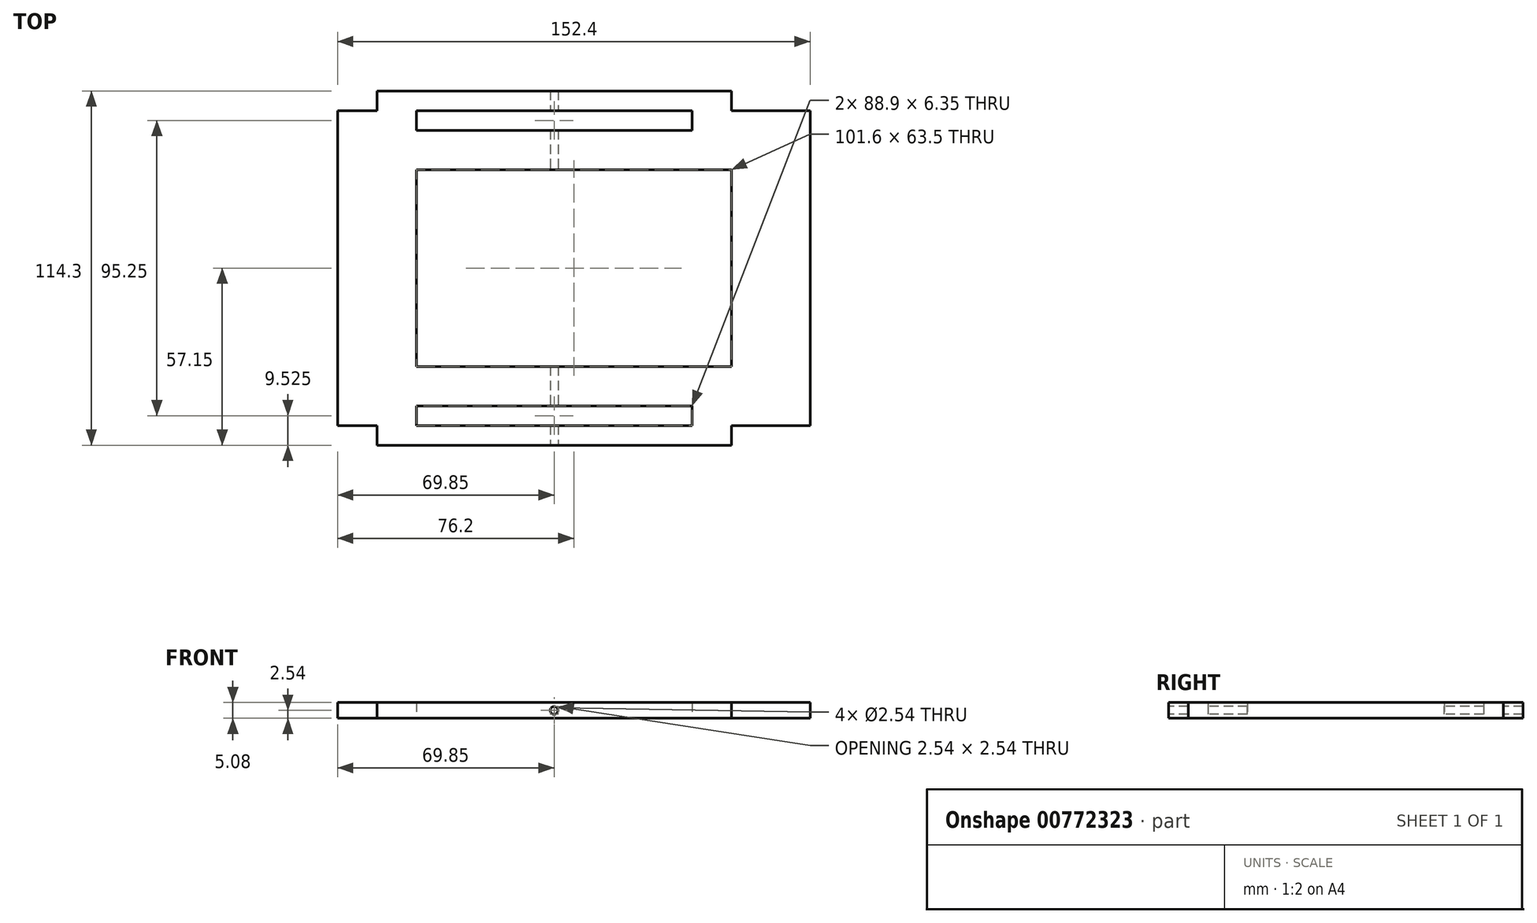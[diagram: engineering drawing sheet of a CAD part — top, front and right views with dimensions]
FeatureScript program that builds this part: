
annotation { "Feature Type Name" : "Feature", "Feature Type Description" : "" }
export const myFeature = defineFeature(function(context is Context, id is Id, definition is map)
    precondition{}
    {
        {
            var Q0;
            Q0=qCreatedBy(makeId("Top.planeOp"),FACE);
            var sketch = newSketch(context, id + "F0", { "sketchPlane" : qUnion([Q0])});
            skLineSegment(sketch, "E0", {"start": v(-76.2, 0) * mm, "end": v(-76.2, 50.8) * mm});
            skLineSegment(sketch, "E1", {"start": v(76.2, 0) * mm, "end": v(76.2, 50.8) * mm});
            skLineSegment(sketch, "E2", {"start": v(-76.2, 0) * mm, "end": v(-76.2, -50.8) * mm});
            skLineSegment(sketch, "E3", {"start": v(76.2, 0) * mm, "end": v(76.2, -50.8) * mm});
            skLineSegment(sketch, "E4", {"start": v(-76.2, -50.8) * mm, "end": v(76.2, -50.8) * mm});
            skLineSegment(sketch, "E5", {"start": v(-76.2, 50.8) * mm, "end": v(76.2, 50.8) * mm});
            skPoint(sketch, "E6", {"position": v(-50.8, -50.8) * mm});
            skPoint(sketch, "E7", {"position": v(38.1, -50.8) * mm});
            skLineSegment(sketch, "E8", {"start": v(-50.8, -50.8) * mm, "end": v(-50.8, -44.45) * mm});
            skLineSegment(sketch, "E9", {"start": v(-50.8, -44.45) * mm, "end": v(38.1, -44.45) * mm});
            skLineSegment(sketch, "E10", {"start": v(38.1, -44.45) * mm, "end": v(38.1, -50.8) * mm});
            skPoint(sketch, "E11", {"position": v(-50.8, 50.8) * mm});
            skPoint(sketch, "E12", {"position": v(38.1, 50.8) * mm});
            skLineSegment(sketch, "E13", {"start": v(-50.8, 50.8) * mm, "end": v(-50.8, 44.45) * mm});
            skLineSegment(sketch, "E14", {"start": v(-50.8, 44.45) * mm, "end": v(38.1, 44.45) * mm});
            skLineSegment(sketch, "E15", {"start": v(38.1, 50.8) * mm, "end": v(38.1, 44.45) * mm});
            skPoint(sketch, "E16", {"position": v(-63.5, -50.8) * mm});
            skPoint(sketch, "E17", {"position": v(50.8, -50.8) * mm});
            skPoint(sketch, "E18", {"position": v(-63.5, 50.8) * mm});
            skPoint(sketch, "E19", {"position": v(50.8, 50.8) * mm});
            skLineSegment(sketch, "E20", {"start": v(-63.5, -50.8) * mm, "end": v(-63.5, -57.15) * mm});
            skLineSegment(sketch, "E21", {"start": v(-63.5, 50.8) * mm, "end": v(-63.5, 57.15) * mm});
            skLineSegment(sketch, "E22", {"start": v(50.8, 50.8) * mm, "end": v(50.8, 57.15) * mm});
            skLineSegment(sketch, "E23", {"start": v(50.8, -50.8) * mm, "end": v(50.8, -57.15) * mm});
            skLineSegment(sketch, "E24", {"start": v(-63.5, 57.15) * mm, "end": v(50.8, 57.15) * mm});
            skLineSegment(sketch, "E25", {"start": v(-63.5, -57.15) * mm, "end": v(50.8, -57.15) * mm});
            skLineSegment(sketch, "E26.bottom", {"start": v(50.8, 31.75) * mm, "end": v(-50.8, 31.75) * mm});
            skLineSegment(sketch, "E26.top", {"start": v(50.8, -31.75) * mm, "end": v(-50.8, -31.75) * mm});
            skLineSegment(sketch, "E26.left", {"start": v(50.8, 31.75) * mm, "end": v(50.8, -31.75) * mm});
            skLineSegment(sketch, "E26.right", {"start": v(-50.8, 31.75) * mm, "end": v(-50.8, -31.75) * mm});
            skSolve(sketch);
        }
        {
            var Q0;
            {var subQ3=sQuery(id+"F0.wireOp",EDGE,"E0");Q0=makeQuery(id+"F0.imprint","IMPRINT",FACE,{"disambiguationData":[TD([[makeQuery(id+"F0.imprint","IMPRINT",EDGE,{"derivedFrom":subQ3}),-1.0]])]});}
            var Q1;
            {var subQ3=sQuery(id+"F0.wireOp",EDGE,"E21");Q1=makeQuery(id+"F0.imprint","IMPRINT",FACE,{"disambiguationData":[TD([[makeQuery(id+"F0.imprint","IMPRINT",EDGE,{"derivedFrom":subQ3}),-1.0]])]});}
            var Q2;
            {var subQ4=sQuery(id+"F0.wireOp",EDGE,"E20");Q2=makeQuery(id+"F0.imprint","IMPRINT",FACE,{"disambiguationData":[TD([[makeQuery(id+"F0.imprint","IMPRINT",EDGE,{"derivedFrom":subQ4}),1.0]])]});}
            extrude(context, id + "F1", {"entities" : qUnion([Q0, Q1, Q2]), "depth" : 5.08 * mm, "offsetDistance" : 25.4 * mm});
        }
        {
            var Q0;
            Q0=makeQuery(id+"F1.opExtrude","SWEPT_FACE",FACE,{"disambiguationData":[OSD([sQuery(id+"F0.wireOp",EDGE,"E25")])]});
            var sketch = newSketch(context, id + "F2", { "sketchPlane" : qUnion([Q0])});
            skLineSegment(sketch, "E27", {"start": v(-6.35, 0) * mm, "end": v(-6.35, 5.08) * mm});
            skCircle(sketch, "E28", {"center": v(-6.35, 2.54) * mm, "radius": 1.27 * mm});
            skSolve(sketch);
        }
        {
            var Q0;
            Q0=qSketchRegion(id+"F2",true);
            extrude(context, id + "F3", {"entities" : qUnion([Q0]), "operationType" : NewBodyOperationType.REMOVE, "oppositeDirection" : true, "depth" : 152.4 * mm, "offsetDistance" : 25.4 * mm});
        }
    });
